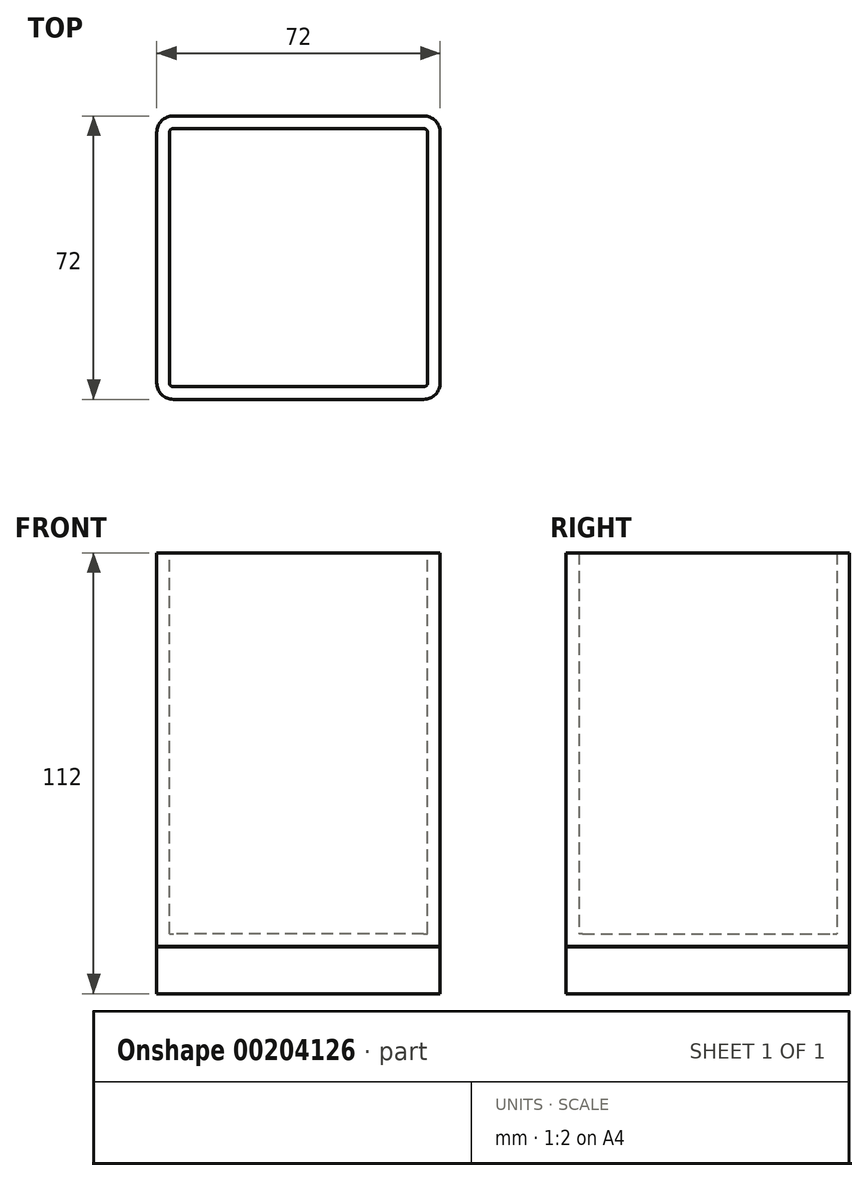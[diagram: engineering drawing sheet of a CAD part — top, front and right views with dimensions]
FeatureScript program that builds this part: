
annotation { "Feature Type Name" : "Feature", "Feature Type Description" : "" }
export const myFeature = defineFeature(function(context is Context, id is Id, definition is map)
    precondition{}
    {
        {
            var Q0;
            Q0=qCreatedBy(makeId("Top.planeOp"),FACE);
            var sketch = newSketch(context, id + "F0", { "sketchPlane" : qUnion([Q0])});
            skLineSegment(sketch, "E0.bottom", {"start": v(36, -36) * mm, "end": v(-36, -36) * mm});
            skLineSegment(sketch, "E0.top", {"start": v(36, 36) * mm, "end": v(-36, 36) * mm});
            skLineSegment(sketch, "E0.left", {"start": v(36, -36) * mm, "end": v(36, 36) * mm});
            skLineSegment(sketch, "E0.right", {"start": v(-36, -36) * mm, "end": v(-36, 36) * mm});
            skPoint(sketch, "E0.middle", {"position": v(0, 0) * mm});
            skSolve(sketch);
        }
        {
            var Q0;
            Q0 = qSketchRegion(id + "F0", true);
            extrude(context, id + "F1", {"entities" : qUnion([Q0]), "depth" : 100 * mm});
        }
        {
            var Q0;
            Q0=makeQuery(id+"F1.opExtrude","SWEPT_EDGE",EDGE,{"disambiguationData":[OSD([sQuery(id+"F0.wireOp",EDGE,"E0.bottom"),sQuery(id+"F0.wireOp",EDGE,"E0.right")])]});
            var Q1;
            Q1=makeQuery(id+"F1.opExtrude","SWEPT_EDGE",EDGE,{"disambiguationData":[OSD([sQuery(id+"F0.wireOp",EDGE,"E0.bottom"),sQuery(id+"F0.wireOp",EDGE,"E0.left")])]});
            var Q2;
            Q2=makeQuery(id+"F1.opExtrude","SWEPT_EDGE",EDGE,{"disambiguationData":[OSD([sQuery(id+"F0.wireOp",EDGE,"E0.top"),sQuery(id+"F0.wireOp",EDGE,"E0.left")])]});
            var Q3;
            Q3=makeQuery(id+"F1.opExtrude","SWEPT_EDGE",EDGE,{"disambiguationData":[OSD([sQuery(id+"F0.wireOp",EDGE,"E0.top"),sQuery(id+"F0.wireOp",EDGE,"E0.right")])]});
            fillet(context, id + "F2", {"entities" : qUnion([Q0, Q1, Q2, Q3]), "radius" : 4.2 * mm, "tangentPropagation" : true, "allowEdgeOverflow" : false});
        }
        {
            var Q0;
            Q0=makeQuery(id+"F1.opExtrude","CAP_FACE",FACE,{"disambiguationData":[OSD([sQuery(id+"F0.wireOp",EDGE,"E0.bottom"),sQuery(id+"F0.wireOp",EDGE,"E0.top"),sQuery(id+"F0.wireOp",EDGE,"E0.left"),sQuery(id+"F0.wireOp",EDGE,"E0.right")])],"isStart":false});
            shell(context, id + "F3", {"entities" : qUnion([Q0]), "thickness" : 3.2 * mm});
        }
        {
            var Q0;
            Q0=makeQuery(id+"F1.opExtrude","CAP_FACE",FACE,{"disambiguationData":[OSD([sQuery(id+"F0.wireOp",EDGE,"E0.bottom"),sQuery(id+"F0.wireOp",EDGE,"E0.top"),sQuery(id+"F0.wireOp",EDGE,"E0.left"),sQuery(id+"F0.wireOp",EDGE,"E0.right")])],"isStart":true});
            var sketch = newSketch(context, id + "F4", { "sketchPlane" : qUnion([Q0])});
            skLineSegment(sketch, "E1.0.0", {"start": v(36, -31.8) * mm, "end": v(36, 31.8) * mm});
            skArc(sketch, "E1.0.1", {"start": v(36, 31.8) * mm, "mid": v(34.77, 34.77) * mm, "end": v(31.8, 36) * mm});
            skLineSegment(sketch, "E1.0.2", {"start": v(31.8, 36) * mm, "end": v(-31.8, 36) * mm});
            skArc(sketch, "E1.0.3", {"start": v(-31.8, 36) * mm, "mid": v(-34.77, 34.77) * mm, "end": v(-36, 31.8) * mm});
            skLineSegment(sketch, "E1.0.4", {"start": v(-36, 31.8) * mm, "end": v(-36, -31.8) * mm});
            skArc(sketch, "E1.0.5", {"start": v(-36, -31.8) * mm, "mid": v(-34.77, -34.77) * mm, "end": v(-31.8, -36) * mm});
            skLineSegment(sketch, "E1.0.6", {"start": v(-31.8, -36) * mm, "end": v(31.8, -36) * mm});
            skArc(sketch, "E1.0.7", {"start": v(31.8, -36) * mm, "mid": v(34.77, -34.77) * mm, "end": v(36, -31.8) * mm});
            skSolve(sketch);
        }
        {
            var Q0;
            Q0 = qSketchRegion(id + "F4", true);
            extrude(context, id + "F5", {"entities" : qUnion([Q0]), "depth" : 12 * mm, "hasSecondDirection" : true, "secondDirectionOppositeDirection" : false, "secondDirectionDepth" : 0.1 * mm});
        }
    });
